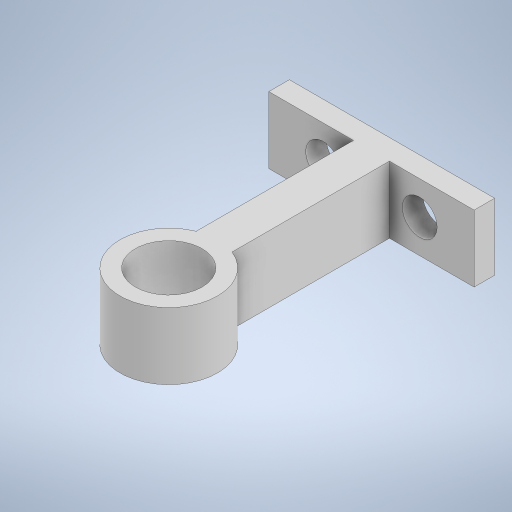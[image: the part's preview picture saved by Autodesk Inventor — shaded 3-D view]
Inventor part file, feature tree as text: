
AUTODESK INVENTOR PART (.ipt)
format: ipt  version: 2023 (Build 270158000, 158)  size: 261,120 bytes
history: native  units: mm
features: extrude x3, sketch x3, other x1, plane x1
ambient origin geometry x8: Origin, YZ Plane, XZ Plane, XY Plane, X Axis, Y Axis, Z Axis, Center Point
bodies: Body1 (feature_tree)
feature tree (8):
  other  "實體1"
  extrude  "擠出1"  Depth=40.0mm
  extrude  "擠出2"  Depth=13.0mm
  plane  "工作平面3"
  extrude  "擠出4"  Depth=6.8mm
  sketch  "草圖1"
  sketch  "草圖3"
  sketch  "草圖5"
